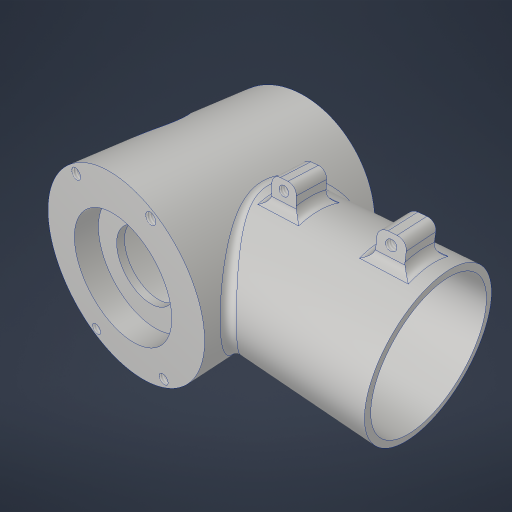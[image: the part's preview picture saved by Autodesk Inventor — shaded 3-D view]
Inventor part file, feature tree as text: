
AUTODESK INVENTOR PART (.ipt)
format: ipt  version: 2023.4 (Build 274418000, 418)  size: 591,360 bytes
history: native  units: in
note: dims shown in document units (in); Inventor stores cm internally (conversion verified against a paired STEP export)
features: sketch x15, extrude x9, plane x7, projected_geometry x6, hole x5, fillet x3
ambient origin geometry x8: Origin, YZ Plane, XZ Plane, XY Plane, X Axis, Y Axis, Z Axis, Center Point
bodies: Solid1 (feature_tree)
feature tree (45):
  extrude  "Extrusion1"  Depth=3.0in TaperAngle=0.0deg
  plane  "Work Plane1"
  extrude  "Extrusion2"  Depth=3.5in
  extrude  "Extrusion3"  Depth=3.0in TaperAngle=0.0deg
  hole  "Hole1"  [1 undecoded]
  plane  "Work Plane2"
  plane  "Work Plane3"
  extrude  "Extrusion5"  Depth=0.5in
  hole  "Hole2"  [1 undecoded]
  extrude  "Extrusion6"  Depth=1.375in
  hole  "Hole3"  [1 undecoded]
  fillet  "Fillet4"  [1 undecoded]
  hole  "Hole5"  [1 undecoded]
  sketch  "Sketch14"  dims[d45=2.375in]
  plane  "Work Plane4"
  extrude  "Extrusion8"  Depth=1.5in
  fillet  "Fillet5"  Radius=0.375in
  plane  "Work Plane5"
  extrude  "Extrusion9"  Depth=1.5in
  plane  "Work Plane6"
  extrude  "Extrusion10"  Depth=0.125in TaperAngle=0.0deg
  fillet  "Fillet6"  [1 undecoded]
  hole  "Hole6"  [1 undecoded]
  plane  "Work Plane7"
  extrude  "Extrusion11"  Depth=0.125in
  sketch  "Sketch1"  dims[d0=3.0in d1=3.0in d2=0.0in]
  sketch  "Sketch2"  dims[d3=3.5in d4=2.06in]
  sketch  "Sketch3"  dims[d5=0.1in d6=3.0in d7=0.0in]
  sketch  "Sketch4"  dims[d8=3.3in d9=0.0in]
  sketch  "Sketch7"  dims[d11=1.125in d12=0.75in d13=1.875in d14=0.375in d15=0.5635in d16=1.625in d17=0.8108in d22=1.5in d27=-1.875in]
  sketch  "Sketch8"  dims[d28=0.375in d29=0.5in]
  sketch  "Sketch9"  dims[d30=1.0in d31=0.0in]
  sketch  "Sketch10"  dims[d34=1.125in d35=0.75in d36=1.875in d37=0.375in d38=0.5635in d39=1.0in d40=0.8108in d41=2.0in d42=0.0in]
  sketch  "Sketch13"  dims[d43=2.744in d44=1.375in]
  sketch  "Sketch15"  dims[d46=0.171in d47=0.432in d48=0.385in d49=0.25in d50=0.5635in d51=1.0in d52=0.8108in d69=0.13in]
  sketch  "Sketch16"  dims[d70=0.156in d71=0.38in d72=0.375in d73=0.25in d74=0.5635in d75=1.0in d76=0.8108in d77=45.0deg]
  sketch  "Sketch17"  dims[d78=1.0in d79=1.0in d80=0.0in]
  sketch  "Sketch18"  dims[d81=0.02in d83=1.5in d84=0.375in]
  sketch  "Sketch19"  dims[d85=0.5in d86=1.5in d87=0.5in d88=0.0in d89=-1.5in d90=0.375in d91=0.5in d92=1.5in d93=0.5in d94=0.0in d95=1.5in d96=1.5in d97=0.13in d98=0.145in d99=0.38in d100=0.385in d101=0.25in d102=0.5635in d103=1.0in d104=0.8108in d105=-2.0in d106=0.1in d107=0.125in d108=0.0in]
  projected_geometry  "Project Cut Edges3"
  projected_geometry  "Project Cut Edges4"
  projected_geometry  "Project Cut Edges5"
  projected_geometry  "Project Cut Edges6"
  projected_geometry  "Project Cut Edges7"
  projected_geometry  "Project Cut Edges8"
note: 7 required parameter values undecoded (feature->parameter linkage not recoverable at this tier; creation-order binding heuristic only, values carry confidence <= 0.55)
